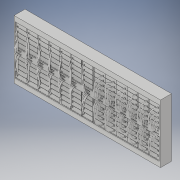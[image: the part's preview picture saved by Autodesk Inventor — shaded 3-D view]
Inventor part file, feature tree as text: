
AUTODESK INVENTOR PART (.ipt)
format: ipt  version: 2017 (Build 210142000, 142)  size: 6,928,384 bytes
history: native  units: in
note: dims shown in document units (in); Inventor stores cm internally (conversion verified against a paired STEP export)
features: sweep x35, sketch x5, extrude x3, mirror x2, plane x2, other x1
ambient origin geometry x8: Origin, YZ Plane, XZ Plane, XY Plane, X Axis, Y Axis, Z Axis, Center Point
bodies: Solid1 (feature_tree)
feature tree (48):
  extrude  "shelfing for towers"  Depth=20.0in
  other  "front of towers workplane"
  extrude  "front of towers"  Depth=0.0833in
  extrude  "towers defined"  Depth=0.5833in
  sketch  "Sketch4"  dims[d7=1.5in d8=2.9167in d9=1.5in d10=0.5833in d11=0.5833in d12=0.0833in d13=0.0833in d35=0.0833in d36=1.5in d37=2.9167in d38=1.5in d39=0.0in d40=-0.1in d47=1.5in d48=0.0in d60=0.5833in d61=0.01in d62=0.5833in d63=0.01in d64=0.5833in d65=0.01in d66=0.5833in d67=0.01in d68=0.01in d69=0.01in d70=0.01in d71=0.01in d72=0.005in d73=0.005in d74=0.005in d75=0.005in d79=0.005in d80=0.005in d81=0.005in d82=0.005in d83=0.005in d84=0.005in d85=0.005in d86=0.005in d88=0.01in d89=0.0in d90=1.5in d91=0.005in d92=0.01in d93=1.5in d94=0.01in d95=1.5in d96=0.01in d97=0.01in d98=1.5in d99=0.01in d100=1.5in d101=0.01in d102=0.01in d103=0.01in d104=0.01in d105=0.01in d106=0.01in d107=0.01in d108=0.01in d109=0.01in d110=0.01in d111=0.005in d112=0.2289in d115=0.125in d116=0.15in d117=0.15in d118=0.15in d119=0.15in d120=0.15in d121=0.125in d122=0.15in d123=0.15in d124=0.15in d125=0.15in d126=1.5in d127=0.125in d128=0.15in d129=0.15in d130=0.15in d131=0.15in d132=1.5in d133=0.125in d134=0.15in d135=0.15in d136=0.15in d137=0.15in d138=1.5in d139=0.125in d140=0.15in d141=0.15in d142=0.15in d143=0.15in d144=1.5in d145=0.125in d146=0.15in d147=0.15in d148=0.15in d149=0.15in d150=1.5in d187=0.125in d188=0.15in d189=0.15in d190=0.15in d191=0.15in d192=1.5in d193=0.2292in d194=0.15in d195=0.15in d196=0.15in d197=0.15in d198=0.15in d273=0.15in d274=0.15in d275=0.15in d276=0.15in d277=0.15in d286=1.5in d287=1.5in d288=1.5in d289=1.5in d290=1.5in d291=0.15in d293=0.15in d294=0.15in d295=0.15in d296=0.15in d297=0.15in d298=0.15in d300=0.15in d301=0.15in d302=0.15in d303=0.15in d304=0.15in d305=0.15in d306=0.15in d307=0.15in d308=0.15in d309=0.15in d310=0.15in d311=0.15in d312=0.15in d313=0.15in d314=0.15in d315=0.15in d316=90.0deg d317=90.0deg d318=0.25in d319=1.5in d320=1.5in d321=1.5in d322=1.5in d323=1.5in d330=1.5in d331=1.5in d332=1.5in d333=1.5in d334=1.5in d340=1.5in d344=1.5in d345=1.5in d346=1.5in d347=1.5in d348=1.5in d353=1.5in d354=1.5in d355=1.5in d356=1.5in d357=1.5in d362=1.5in d364=1.5in d366=1.5in d367=1.5in d368=1.5in d369=1.5in d370=1.5in d376=1.5in d377=1.5in d378=1.5in d379=1.5in d380=1.5in d386=1.5in d387=1.5in d388=1.5in d389=1.5in d390=1.5in d395=1.5in d396=1.5in d397=1.5in d398=1.5in d399=1.5in d404=1.5in d406=1.5in d408=1.5in d410=1.5in d411=0.5833in d527=0.125in d529=0.5833in d530=0.5833in d531=0.5833in d532=0.5833in d537=0.15in d538=0.3937in d539=0.3937in d540=0.3937in d541=0.3937in d542=0.3937in d543=0.3937in d544=0.3937in d545=0.3937in d546=0.3937in d547=0.3937in d548=0.0in d549=0.0in d550=0.0in d551=0.0in d552=0.0in d553=0.0in d554=0.0in d555=0.0in d556=0.3937in d557=0.3937in d558=0.0in d559=0.0in d560=0.0in d561=0.0in d562=0.3937in d563=0.3937in d564=0.3937in d565=0.3937in d566=0.3937in d567=0.3937in d568=0.3937in d569=0.3937in d570=0.0in d571=0.0in d572=0.0in d573=0.0in d574=0.0in d575=0.0in d576=0.0in d577=0.0in d578=0.3937in d579=0.3937in d580=0.3937in d581=0.3937in d582=0.3937in d583=0.3937in d584=0.3937in d585=0.3937in d586=0.3937in d587=0.3937in d588=0.0in d589=0.0in d590=0.0in d591=0.0in d592=0.0in d593=0.0in d594=0.0in d595=0.0in d596=0.0in d597=0.0in d598=0.06in d600=1.5in d601=0.3937in d602=0.3937in d603=0.3937in d604=0.3937in d605=0.3937in d606=0.3937in d607=0.3937in d608=0.3937in d609=0.3937in d610=0.3937in d611=0.3937in d612=0.3937in d613=0.3937in d614=0.3937in d615=0.3937in d616=0.3937in d617=0.3937in d618=0.3937in d619=0.3937in d620=0.3937in d621=0.06in d622=0.3937in d623=0.3937in d624=0.3937in d625=0.3937in d626=0.3937in d627=0.3937in d628=0.3937in d629=0.3937in d630=0.3937in d631=0.3937in d632=0.0in d633=0.0in d634=0.0in d635=0.0in d636=0.0in d637=0.0in d638=0.0in d639=0.0in d640=0.0in d641=0.0in d642=0.0in d643=0.0in d644=0.0in d645=0.0in d646=0.0in d647=0.0in d648=0.0in d649=0.0in d650=0.0in d651=0.0in d652=0.0in d653=0.0in d654=0.0in d655=0.0in d656=0.0in d657=0.0in d658=0.0in d659=0.0in d660=0.0in d661=0.0in d662=0.125in d663=0.25in d664=0.5833in d665=0.5833in d666=0.5833in d667=0.5833in d668=0.3937in d669=0.3937in d670=0.3937in d671=0.3937in d672=0.3937in d673=0.3937in d674=0.3937in d675=0.3937in d676=0.3937in d677=0.3937in d678=0.0in d679=0.0in d680=0.0in d681=0.0in d682=0.0in d683=0.0in d684=0.0in d685=0.0in d686=0.0in d687=0.0in]
  sketch  "3D Sketch1"
  sweep  "cable 1"
  sweep  "cable 2"
  sweep  "cable 3"
  sweep  "cable 4"
  sweep  "cable 5"
  sweep  "cable 6"
  sweep  "cable 7"
  sweep  "cable 8"
  sweep  "cable 9"
  sweep  "cable 10"
  sweep  "cable 11"
  sweep  "cable 12"
  sweep  "cable 13"
  sweep  "cable 14"
  sweep  "cable 15"
  sweep  "cable 16"
  sweep  "cable 17"
  sweep  "cable 18"
  sweep  "cable 19"
  sweep  "cable 20"
  sweep  "cable 21"
  sweep  "cable 22"
  sweep  "cable 23"
  sweep  "cable 24"
  sweep  "cable 25"
  sweep  "cable 26"
  sweep  "cable 27"
  sweep  "cable 28"
  sweep  "cable 29"
  sweep  "cable 30"
  sweep  "cable 31"
  sweep  "cable 32"
  sweep  "cable 33"
  sweep  "cable 34"
  sweep  "cable 35"
  mirror  "Mirror1"
  mirror  "Mirror2"
  sketch  "Sketch1"  dims[d0=8.0in d1=20.0in]
  sketch  "Sketch2"  dims[d2=0.0833in d4=0.0833in]
  sketch  "Sketch3"  dims[d5=0.0833in d6=0.5833in]
  plane  "Work Plane2"
  plane  "Work Plane3"
